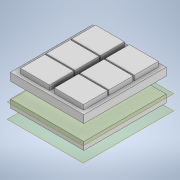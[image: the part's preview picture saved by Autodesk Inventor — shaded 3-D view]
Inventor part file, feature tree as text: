
AUTODESK INVENTOR PART (.ipt)
format: ipt  version: 2020 (Build 240168000, 168)  size: 173,568 bytes
history: native  units: mm
features: extrude x5, sketch x5, plane x2
ambient origin geometry x8: Origin, YZ Plane, XZ Plane, XY Plane, X Axis, Y Axis, Z Axis, Center Point
bodies: Solid1 (feature_tree)
feature tree (12):
  extrude  "Extrusion1"  Depth=17.0mm
  extrude  "Extrusion2"  Depth=7.15mm
  plane  "Work Plane1"
  extrude  "Extrusion3"  Depth=5.0mm
  plane  "Work Plane2"
  extrude  "Extrusion4"  Depth=5.0mm
  extrude  "Extrusion5"  Depth=0.25mm
  sketch  "Sketch1"  dims[d0=17.0mm d1=14.3mm]
  sketch  "Sketch2"  dims[d2=8.5mm d3=7.15mm]
  sketch  "Sketch3"  dims[d4=1.6mm d5=0.0mm d6=5.0mm]
  sketch  "Sketch4"  dims[d7=6.0mm d8=5.0mm]
  sketch  "Sketch5"  dims[d9=5.0mm d10=0.25mm d11=0.25mm d12=0.75mm d13=5.0mm d14=5.0mm d15=5.0mm d16=6.0mm d17=6.0mm d18=6.0mm d19=0.25mm d20=0.25mm d21=1.0mm d22=0.45mm d23=1.0mm d24=0.0mm d25=3.2mm d26=1.6mm d27=0.0mm d28=1.5mm d29=0.89mm d30=0.0mm d31=0.89mm d32=0.0mm]
